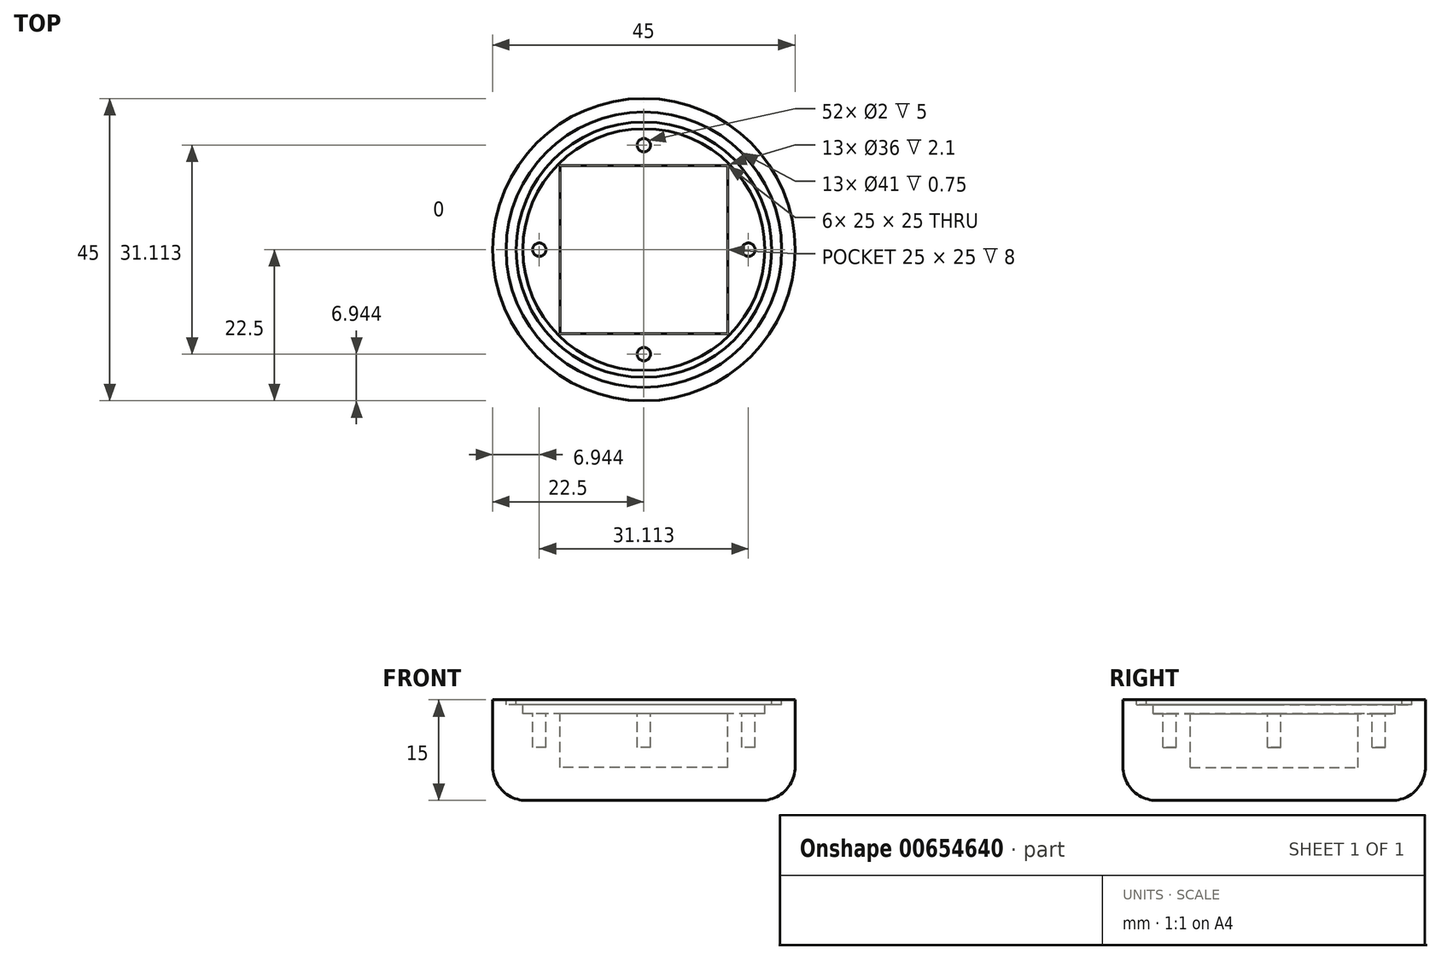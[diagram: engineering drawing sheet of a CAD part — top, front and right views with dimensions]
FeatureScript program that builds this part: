
annotation { "Feature Type Name" : "Feature", "Feature Type Description" : "" }
export const myFeature = defineFeature(function(context is Context, id is Id, definition is map)
    precondition{}
    {
        {
            var Q0;
            Q0=qCreatedBy(makeId("Top.planeOp"),FACE);
            var sketch = newSketch(context, id + "F0", { "sketchPlane" : qUnion([Q0])});
            skCircle(sketch, "E0", {"center": v(0, 0) * mm, "radius": 22.5 * mm});
            skSolve(sketch);
        }
        {
            var Q0;
            Q0 = qSketchRegion(id + "F0", true);
            extrude(context, id + "F1", {"entities" : qUnion([Q0]), "depth" : 15 * mm, "offsetDistance" : 25 * mm});
        }
        {
            var Q0;
            Q0=makeQuery(id+"F1.opExtrude","CAP_FACE",FACE,{"disambiguationData":[OSD([sQuery(id+"F0.wireOp",EDGE,"E0")])],"isStart":false});
            var sketch = newSketch(context, id + "F2", { "sketchPlane" : qUnion([Q0])});
            skCircle(sketch, "E1", {"center": v(0, 0) * mm, "radius": 18 * mm});
            skSolve(sketch);
        }
        {
            var Q0;
            Q0 = qSketchRegion(id + "F2", true);
            extrude(context, id + "F3", {"entities" : qUnion([Q0]), "operationType" : NewBodyOperationType.REMOVE, "oppositeDirection" : true, "depth" : 2.1 * mm, "offsetDistance" : 25 * mm});
        }
        {
            var Q0;
            Q0=makeQuery(id+"F3.boolean.opBoolean","COPY",FACE,{"derivedFrom":makeQuery(id+"F3.opExtrude","CAP_FACE",FACE,{"disambiguationData":[OSD([sQuery(id+"F2.wireOp",EDGE,"E1")])],"isStart":false})});
            var sketch = newSketch(context, id + "F4", { "sketchPlane" : qUnion([Q0])});
            skLineSegment(sketch, "E2.bottom", {"start": v(12.5, -12.5) * mm, "end": v(-12.5, -12.5) * mm});
            skLineSegment(sketch, "E2.top", {"start": v(12.5, 12.5) * mm, "end": v(-12.5, 12.5) * mm});
            skLineSegment(sketch, "E2.left", {"start": v(12.5, -12.5) * mm, "end": v(12.5, 12.5) * mm});
            skLineSegment(sketch, "E2.right", {"start": v(-12.5, -12.5) * mm, "end": v(-12.5, 12.5) * mm});
            skPoint(sketch, "E2.middle", {"position": v(0, 0) * mm});
            skSolve(sketch);
        }
        {
            var Q0;
            Q0 = qSketchRegion(id + "F4", true);
            extrude(context, id + "F5", {"entities" : qUnion([Q0]), "operationType" : NewBodyOperationType.REMOVE, "oppositeDirection" : true, "depth" : 8 * mm, "offsetDistance" : 25 * mm});
        }
        {
            var Q0;
            Q0=makeQuery(id+"F1.opExtrude","CAP_EDGE",EDGE,{"disambiguationData":[OSD([sQuery(id+"F0.wireOp",EDGE,"E0")])],"isStart":true});
            fillet(context, id + "F6", {"entities" : qUnion([Q0]), "radius" : 5 * mm, "tangentPropagation" : true, "allowEdgeOverflow" : false});
        }
        {
            var Q0;
            Q0=makeQuery(id+"F3.boolean.opBoolean","COPY",FACE,{"derivedFrom":makeQuery(id+"F3.opExtrude","CAP_FACE",FACE,{"disambiguationData":[OSD([sQuery(id+"F2.wireOp",EDGE,"E1")])],"isStart":false})});
            var sketch = newSketch(context, id + "F7", { "sketchPlane" : qUnion([Q0])});
            skCircle(sketch, "E3", {"center": v(0, 15.56) * mm, "radius": 1 * mm});
            skLineSegment(sketch, "E4", {"start": v(0, 0) * mm, "end": v(0, 15.56) * mm, "construction": true});
            skCircle(sketch, "E5", {"center": v(15.56, 0) * mm, "radius": 1 * mm});
            skLineSegment(sketch, "E6", {"start": v(0, 0) * mm, "end": v(15.56, 0) * mm, "construction": true});
            skCircle(sketch, "E7.MirrorC", {"center": v(-15.56, 0) * mm, "radius": 1 * mm});
            skCircle(sketch, "E8.MirrorC", {"center": v(0, -15.56) * mm, "radius": 1 * mm});
            skSolve(sketch);
        }
        {
            var Q0;
            Q0 = qSketchRegion(id + "F7", true);
            extrude(context, id + "F8", {"entities" : qUnion([Q0]), "operationType" : NewBodyOperationType.REMOVE, "oppositeDirection" : true, "depth" : 5 * mm, "offsetDistance" : 25 * mm});
        }
        {
            var Q0;
            Q0=makeQuery(id+"F1.opExtrude","CAP_FACE",FACE,{"disambiguationData":[OSD([sQuery(id+"F0.wireOp",EDGE,"E0")])],"isStart":false});
            var sketch = newSketch(context, id + "F9", { "sketchPlane" : qUnion([Q0])});
            skCircle(sketch, "E9", {"center": v(0, 0) * mm, "radius": 20.5 * mm});
            skCircle(sketch, "E10", {"center": v(0, 0) * mm, "radius": 19 * mm});
            skSolve(sketch);
        }
        {
            var Q0;
            Q0 = qSketchRegion(id + "F9", true);
            extrude(context, id + "F10", {"entities" : qUnion([Q0]), "operationType" : NewBodyOperationType.REMOVE, "oppositeDirection" : true, "depth" : 0.75 * mm, "offsetDistance" : 25 * mm});
        }
    });
